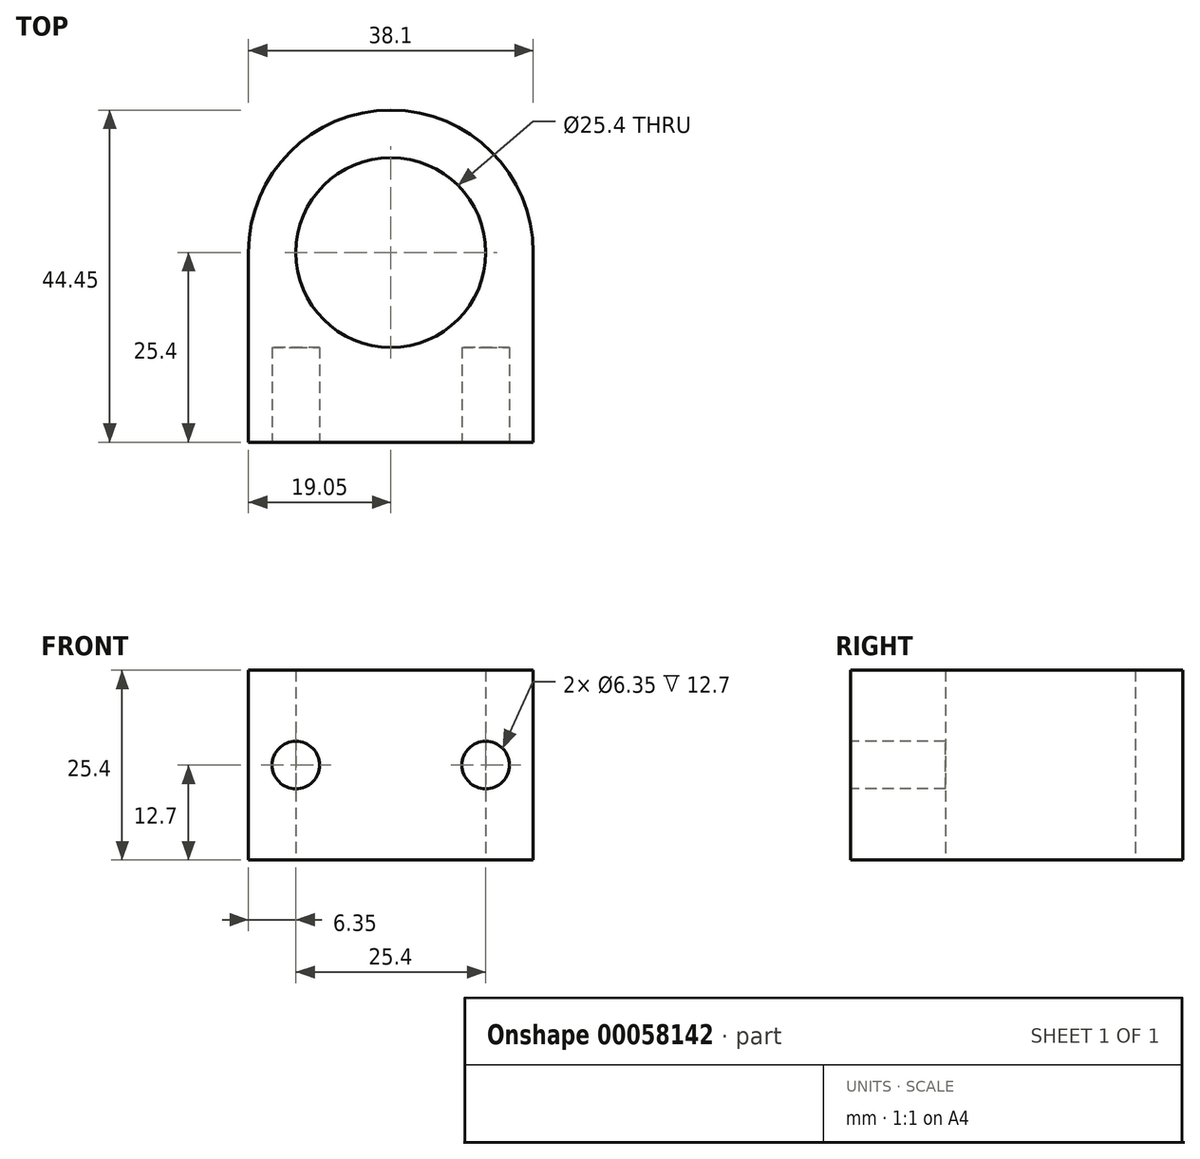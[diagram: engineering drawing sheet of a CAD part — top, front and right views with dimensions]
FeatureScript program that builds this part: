
annotation { "Feature Type Name" : "Feature", "Feature Type Description" : "" }
export const myFeature = defineFeature(function(context is Context, id is Id, definition is map)
    precondition{}
    {
        {
            var Q0;
            Q0=qCreatedBy(makeId("Top.planeOp"),FACE);
            var sketch = newSketch(context, id + "F0", { "sketchPlane" : qUnion([Q0])});
            skCircle(sketch, "E0", {"center": v(0, 0) * mm, "radius": 12.7 * mm});
            skArc(sketch, "E1", {"start": v(19.05, 0) * mm, "mid": v(0, 19.05) * mm, "end": v(-19.05, 0) * mm});
            skLineSegment(sketch, "E2", {"start": v(-19.05, 0) * mm, "end": v(-19.05, -25.4) * mm});
            skLineSegment(sketch, "E3", {"start": v(-19.05, -25.4) * mm, "end": v(19.05, -25.4) * mm});
            skLineSegment(sketch, "E4", {"start": v(19.05, -25.4) * mm, "end": v(19.05, 0) * mm});
            skSolve(sketch);
        }
        {
            var Q0;
            Q0=makeQuery(id+"F0.imprint","IMPRINT",FACE,{"disambiguationData":[TD([[makeQuery(id+"F0.imprint","IMPRINT",EDGE,{"derivedFrom":sQuery(id+"F0.wireOp",EDGE,"E0")}),-1.0]])]});
            extrude(context, id + "F1", {"entities" : qUnion([Q0]), "depth" : 12.7 * mm, "hasSecondDirection" : true, "secondDirectionOppositeDirection" : true, "secondDirectionDepth" : 12.7 * mm});
        }
        {
            var Q0;
            Q0=makeQuery(id+"F1.opExtrude","SWEPT_FACE",FACE,{"disambiguationData":[OSD([sQuery(id+"F0.wireOp",EDGE,"E3")])]});
            var sketch = newSketch(context, id + "F2", { "sketchPlane" : qUnion([Q0])});
            skCircle(sketch, "E5", {"center": v(-12.7, 0) * mm, "radius": 3.18 * mm});
            skCircle(sketch, "E6", {"center": v(12.7, 0) * mm, "radius": 3.18 * mm});
            skSolve(sketch);
        }
        {
            var Q0;
            Q0=makeQuery(id+"F2.imprint","IMPRINT",FACE,{"disambiguationData":[TD([[makeQuery(id+"F2.imprint","IMPRINT",EDGE,{"derivedFrom":sQuery(id+"F2.wireOp",EDGE,"E5")}),1.0]])]});
            var Q1;
            Q1=makeQuery(id+"F2.imprint","IMPRINT",FACE,{"disambiguationData":[TD([[makeQuery(id+"F2.imprint","IMPRINT",EDGE,{"derivedFrom":sQuery(id+"F2.wireOp",EDGE,"E6")}),1.0]])]});
            extrude(context, id + "F3", {"entities" : qUnion([Q0, Q1]), "operationType" : NewBodyOperationType.REMOVE, "oppositeDirection" : true, "depth" : 12.7 * mm});
        }
    });
